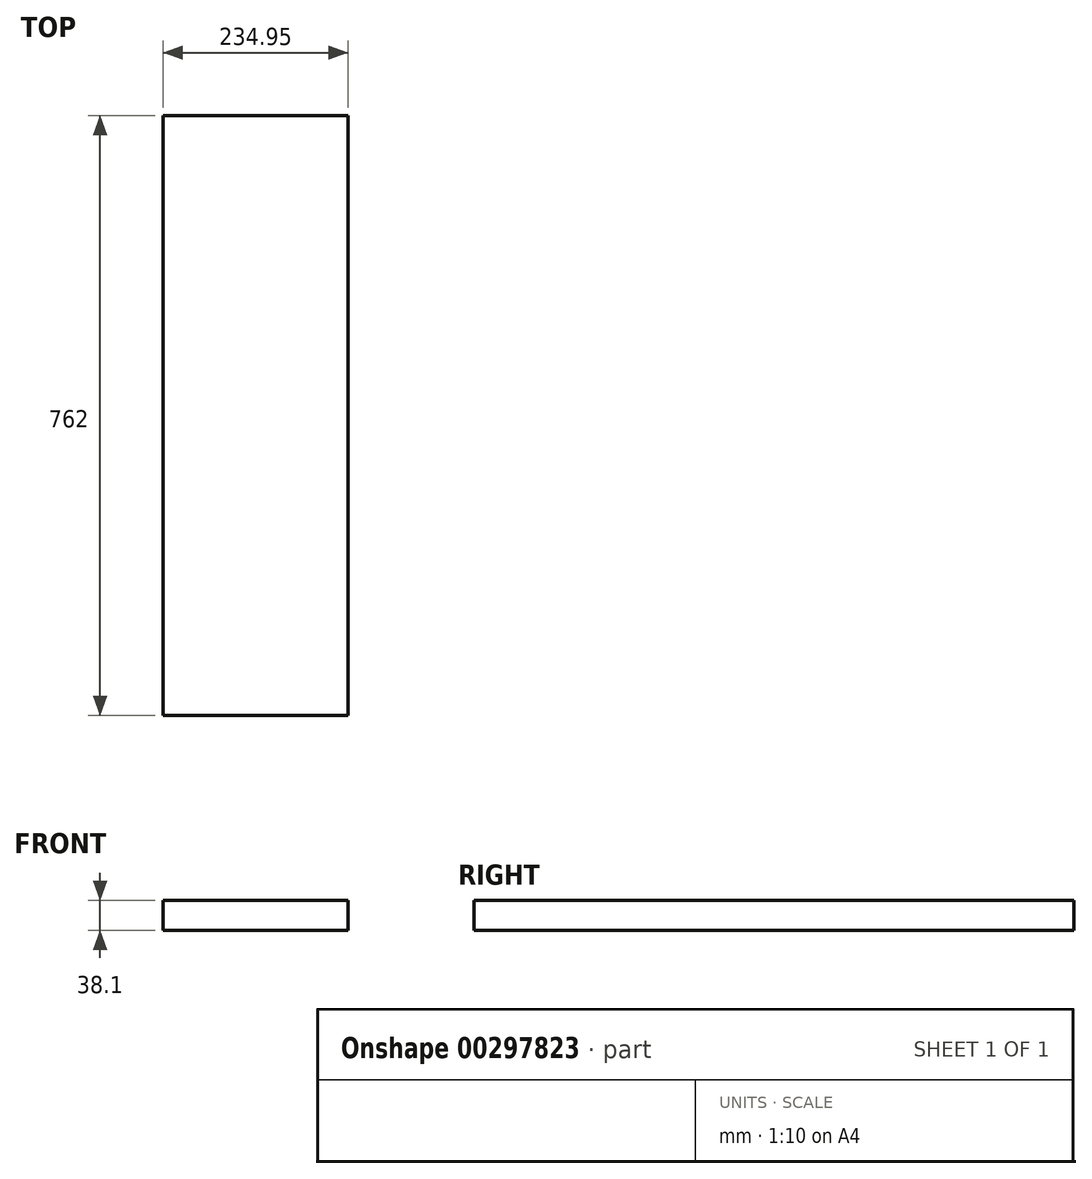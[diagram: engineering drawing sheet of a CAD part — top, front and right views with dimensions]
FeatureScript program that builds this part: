
annotation { "Feature Type Name" : "Feature", "Feature Type Description" : "" }
export const myFeature = defineFeature(function(context is Context, id is Id, definition is map)
    precondition{}
    {
        {
            var Q0;
            Q0=qCreatedBy(makeId("Top.planeOp"),FACE);
            var sketch = newSketch(context, id + "F0", { "sketchPlane" : qUnion([Q0])});
            skLineSegment(sketch, "E0.bottom", {"start": v(0, 0) * mm, "end": v(234.95, 0) * mm});
            skLineSegment(sketch, "E0.top", {"start": v(0, 762) * mm, "end": v(234.95, 762) * mm});
            skLineSegment(sketch, "E0.left", {"start": v(0, 0) * mm, "end": v(0, 762) * mm});
            skLineSegment(sketch, "E0.right", {"start": v(234.95, 0) * mm, "end": v(234.95, 762) * mm});
            skSolve(sketch);
        }
        {
            var Q0;
            Q0=makeQuery(id+"F0.imprint","IMPRINT",FACE,{"disambiguationData":[TD([[makeQuery(id+"F0.imprint","IMPRINT",EDGE,{"derivedFrom":sQuery(id+"F0.wireOp",EDGE,"E0.bottom")}),1.0]])]});
            extrude(context, id + "F1", {"entities" : qUnion([Q0]), "depth" : 38.1 * mm});
        }
    });
